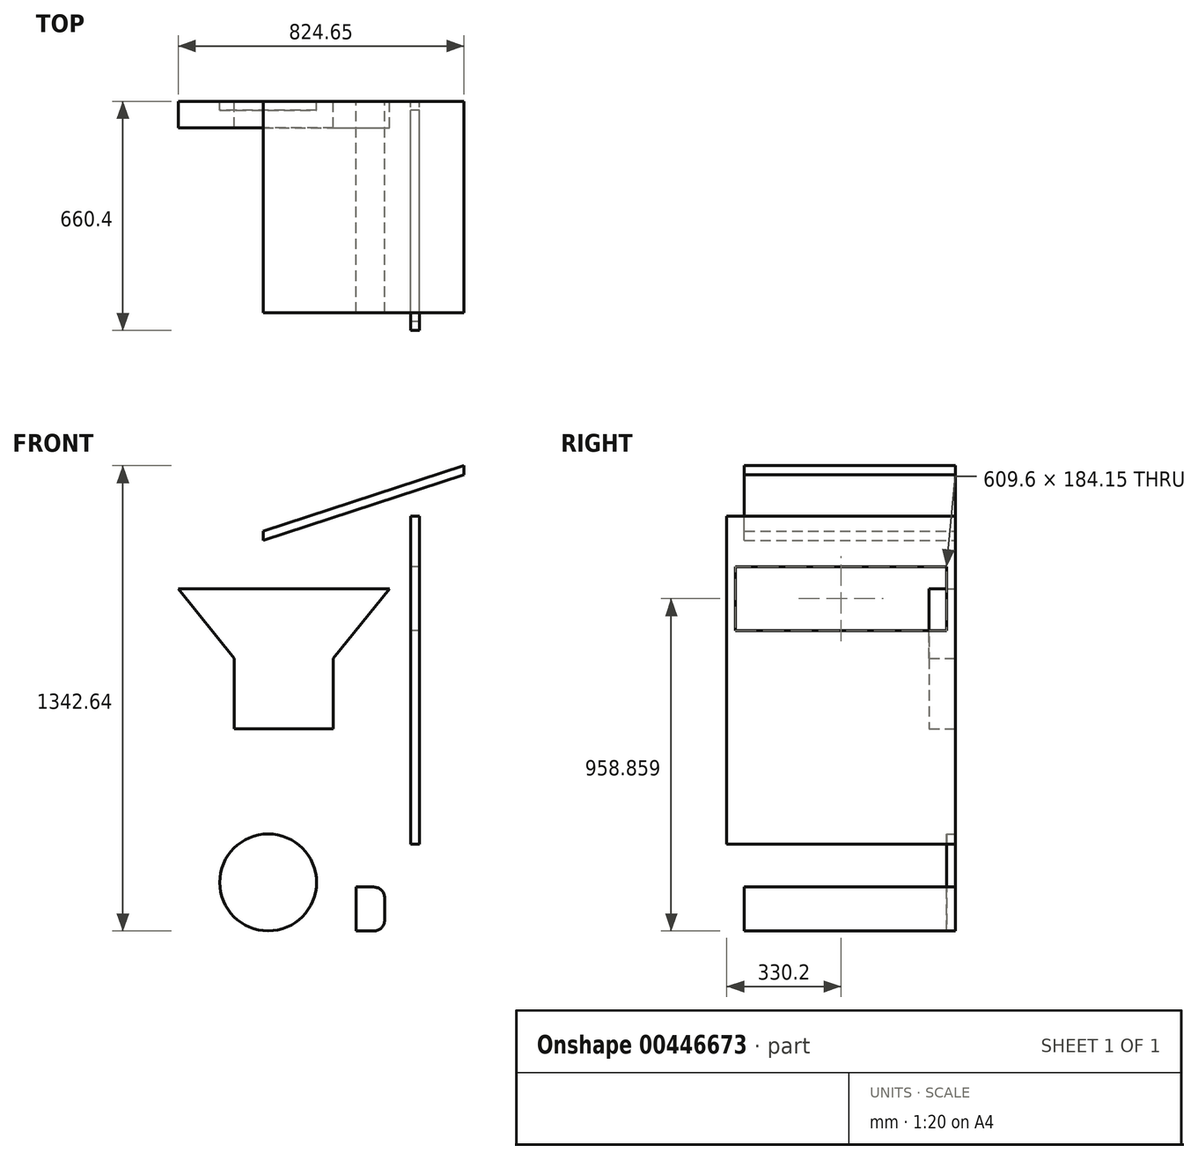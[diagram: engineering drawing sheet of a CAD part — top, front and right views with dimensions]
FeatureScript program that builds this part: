
annotation { "Feature Type Name" : "Feature", "Feature Type Description" : "" }
export const myFeature = defineFeature(function(context is Context, id is Id, definition is map)
    precondition{}
    {
        {
            var Q0;
            Q0=qCreatedBy(makeId("Front.planeOp"),FACE);
            var sketch = newSketch(context, id + "F0", { "sketchPlane" : qUnion([Q0])});
            skLineSegment(sketch, "E0.bottom", {"start": v(0, 0) * mm, "end": v(127, 0) * mm});
            skLineSegment(sketch, "E0.top", {"start": v(0, 635) * mm, "end": v(127, 635) * mm});
            skLineSegment(sketch, "E0.left", {"start": v(0, 0) * mm, "end": v(0, 635) * mm});
            skLineSegment(sketch, "E0.right", {"start": v(127, 0) * mm, "end": v(127, 635) * mm});
            skLineSegment(sketch, "E1", {"start": v(-132.86, 591.83) * mm, "end": v(132.86, 678.17) * mm});
            skLineSegment(sketch, "E2.bottom", {"start": v(0, 0) * mm, "end": v(-82.55, 0) * mm});
            skLineSegment(sketch, "E2.top", {"start": v(0, 127) * mm, "end": v(-82.55, 127) * mm});
            skLineSegment(sketch, "E2.left", {"start": v(0, 0) * mm, "end": v(0, 127) * mm});
            skLineSegment(sketch, "E2.right", {"start": v(-82.55, 0) * mm, "end": v(-82.55, 127) * mm});
            skLineSegment(sketch, "E3.bottom", {"start": v(-82.55, 0) * mm, "end": v(-158.75, 0) * mm});
            skLineSegment(sketch, "E3.top", {"start": v(-82.55, 596.9) * mm, "end": v(-158.75, 596.9) * mm});
            skLineSegment(sketch, "E3.left", {"start": v(-82.55, 0) * mm, "end": v(-82.55, 596.9) * mm});
            skLineSegment(sketch, "E3.right", {"start": v(-158.75, 0) * mm, "end": v(-158.75, 596.9) * mm});
            skLineSegment(sketch, "E4", {"start": v(0, 635) * mm, "end": v(-23.16, 706.3) * mm});
            skLineSegment(sketch, "E5.0", {"start": v(132.86, 678.17) * mm, "end": v(117.16, 726.48) * mm});
            skLineSegment(sketch, "E6.0", {"start": v(-132.86, 591.83) * mm, "end": v(-148.56, 640.14) * mm});
            skLineSegment(sketch, "E7.0", {"start": v(-148.56, 640.14) * mm, "end": v(117.16, 726.48) * mm});
            skCircle(sketch, "E8", {"center": v(0, 635) * mm, "radius": 146.7 * mm});
            skLineSegment(sketch, "E9.0", {"start": v(-82.55, 444.5) * mm, "end": v(-158.75, 444.5) * mm});
            skLineSegment(sketch, "E10", {"start": v(-158.75, 444.5) * mm, "end": v(-209.13, 599.54) * mm});
            skCircle(sketch, "E11", {"center": v(-813.83, 145.7) * mm, "radius": 139.7 * mm});
            skLineSegment(sketch, "E12.bottom", {"start": v(-559.95, 5.39) * mm, "end": v(-509.15, 5.39) * mm});
            skLineSegment(sketch, "E12.top", {"start": v(-559.95, 132.39) * mm, "end": v(-509.15, 132.39) * mm});
            skLineSegment(sketch, "E12.left", {"start": v(-559.95, 5.39) * mm, "end": v(-559.95, 132.39) * mm});
            skLineSegment(sketch, "E12.right", {"start": v(-477.4, 37.14) * mm, "end": v(-477.4, 100.64) * mm});
            skPoint(sketch, "E13.visualSharp", {"position": v(-477.4, 132.39) * mm});
            skArc(sketch, "E13.filletArc", {"start": v(-477.4, 100.64) * mm, "mid": v(-486.7, 123.09) * mm, "end": v(-509.15, 132.39) * mm});
            skPoint(sketch, "E14.visualSharp", {"position": v(-477.4, 5.39) * mm});
            skArc(sketch, "E14.filletArc", {"start": v(-509.15, 5.39) * mm, "mid": v(-486.7, 14.69) * mm, "end": v(-477.4, 37.14) * mm});
            skLineSegment(sketch, "E15.bottom", {"start": v(-403.01, 255.63) * mm, "end": v(-377.61, 255.63) * mm});
            skLineSegment(sketch, "E15.left", {"start": v(-403.01, 255.63) * mm, "end": v(-403.01, 1201.78) * mm});
            skLineSegment(sketch, "E15.right", {"start": v(-377.61, 255.63) * mm, "end": v(-377.61, 1201.78) * mm});
            skLineSegment(sketch, "E16", {"start": v(176.75, 1079) * mm, "end": v(184.6, 1054.85) * mm});
            skLineSegment(sketch, "E17.0", {"start": v(-377.61, 1201.78) * mm, "end": v(-403.01, 1201.78) * mm});
            skLineSegment(sketch, "E18", {"start": v(-828.37, 1159.66) * mm, "end": v(-248.61, 1348.03) * mm});
            skLineSegment(sketch, "E19.0", {"start": v(-828.37, 1132.95) * mm, "end": v(-248.61, 1321.33) * mm});
            skLineSegment(sketch, "E20", {"start": v(-828.37, 1132.95) * mm, "end": v(-828.37, 1159.66) * mm});
            skLineSegment(sketch, "E21", {"start": v(-248.61, 1348.03) * mm, "end": v(-248.61, 1321.33) * mm});
            skLineSegment(sketch, "E22", {"start": v(-1073.26, 993.28) * mm, "end": v(-463.66, 993.28) * mm});
            skLineSegment(sketch, "E23", {"start": v(-625.58, 588.85) * mm, "end": v(-911.33, 588.85) * mm});
            skLineSegment(sketch, "E24", {"start": v(-625.58, 792.05) * mm, "end": v(-463.66, 993.28) * mm});
            skLineSegment(sketch, "E25", {"start": v(-1073.26, 993.28) * mm, "end": v(-911.33, 792.05) * mm});
            skLineSegment(sketch, "E26", {"start": v(-911.33, 792.05) * mm, "end": v(-911.33, 588.85) * mm});
            skLineSegment(sketch, "E27", {"start": v(-625.58, 792.05) * mm, "end": v(-625.58, 588.85) * mm});
            skLineSegment(sketch, "E28.0", {"start": v(-1073.26, 396.38) * mm, "end": v(-463.66, 396.38) * mm});
            skSolve(sketch);
        }
        {
            var Q0;
            Q0=makeQuery(id+"F0.imprint","IMPRINT",FACE,{"disambiguationData":[TD([[makeQuery(id+"F0.imprint","IMPRINT",EDGE,{"derivedFrom":sQuery(id+"F0.wireOp",EDGE,"E11")}),1.0]])]});
            extrude(context, id + "F1", {"entities" : qUnion([Q0]), "depth" : 25.4 * mm});
        }
        {
            var Q0;
            Q0=makeQuery(id+"F0.imprint","IMPRINT",FACE,{"disambiguationData":[TD([[makeQuery(id+"F0.imprint","IMPRINT",EDGE,{"derivedFrom":sQuery(id+"F0.wireOp",EDGE,"E12.bottom")}),1.0]])]});
            extrude(context, id + "F2", {"entities" : qUnion([Q0]), "depth" : 609.6 * mm});
        }
        {
            var Q0;
            Q0=makeQuery(id+"F0.imprint","IMPRINT",FACE,{"disambiguationData":[TD([[makeQuery(id+"F0.imprint","IMPRINT",EDGE,{"derivedFrom":sQuery(id+"F0.wireOp",EDGE,"E15.bottom")}),1.0]])]});
            extrude(context, id + "F3", {"entities" : qUnion([Q0]), "depth" : 660.4 * mm});
        }
        {
            var Q0;
            Q0=makeQuery(id+"F3.opExtrude","SWEPT_FACE",FACE,{"disambiguationData":[OSD([sQuery(id+"F0.wireOp",EDGE,"E15.left")])]});
            var sketch = newSketch(context, id + "F4", { "sketchPlane" : qUnion([Q0])});
            skLineSegment(sketch, "E29.0", {"start": v(635, 1056.32) * mm, "end": v(25.4, 1056.32) * mm});
            skLineSegment(sketch, "E30.0", {"start": v(25.4, 872.17) * mm, "end": v(25.4, 1056.32) * mm});
            skLineSegment(sketch, "E31.0", {"start": v(635, 872.17) * mm, "end": v(635, 1056.32) * mm});
            skLineSegment(sketch, "E32.0", {"start": v(635, 872.17) * mm, "end": v(25.4, 872.17) * mm});
            skSolve(sketch);
        }
        {
            var Q0;
            Q0=makeQuery(id+"F4.imprint","IMPRINT",FACE,{"disambiguationData":[TD([[makeQuery(id+"F4.imprint","IMPRINT",EDGE,{"derivedFrom":sQuery(id+"F4.wireOp",EDGE,"E29.0")}),1.0]])]});
            extrude(context, id + "F5", {"entities" : qUnion([Q0]), "operationType" : NewBodyOperationType.REMOVE, "oppositeDirection" : true, "depth" : 27.94 * mm});
        }
        {
            var Q0;
            Q0=makeQuery(id+"F0.imprint","IMPRINT",FACE,{"disambiguationData":[TD([[makeQuery(id+"F0.imprint","IMPRINT",EDGE,{"derivedFrom":sQuery(id+"F0.wireOp",EDGE,"E18")}),-1.0]])]});
            extrude(context, id + "F6", {"entities" : qUnion([Q0]), "depth" : 609.6 * mm});
        }
        {
            var Q0;
            Q0=makeQuery(id+"F0.imprint","IMPRINT",FACE,{"disambiguationData":[TD([[makeQuery(id+"F0.imprint","IMPRINT",EDGE,{"derivedFrom":sQuery(id+"F0.wireOp",EDGE,"E22")}),-1.0]])]});
            extrude(context, id + "F7", {"entities" : qUnion([Q0]), "depth" : 76.2 * mm});
        }
    });
